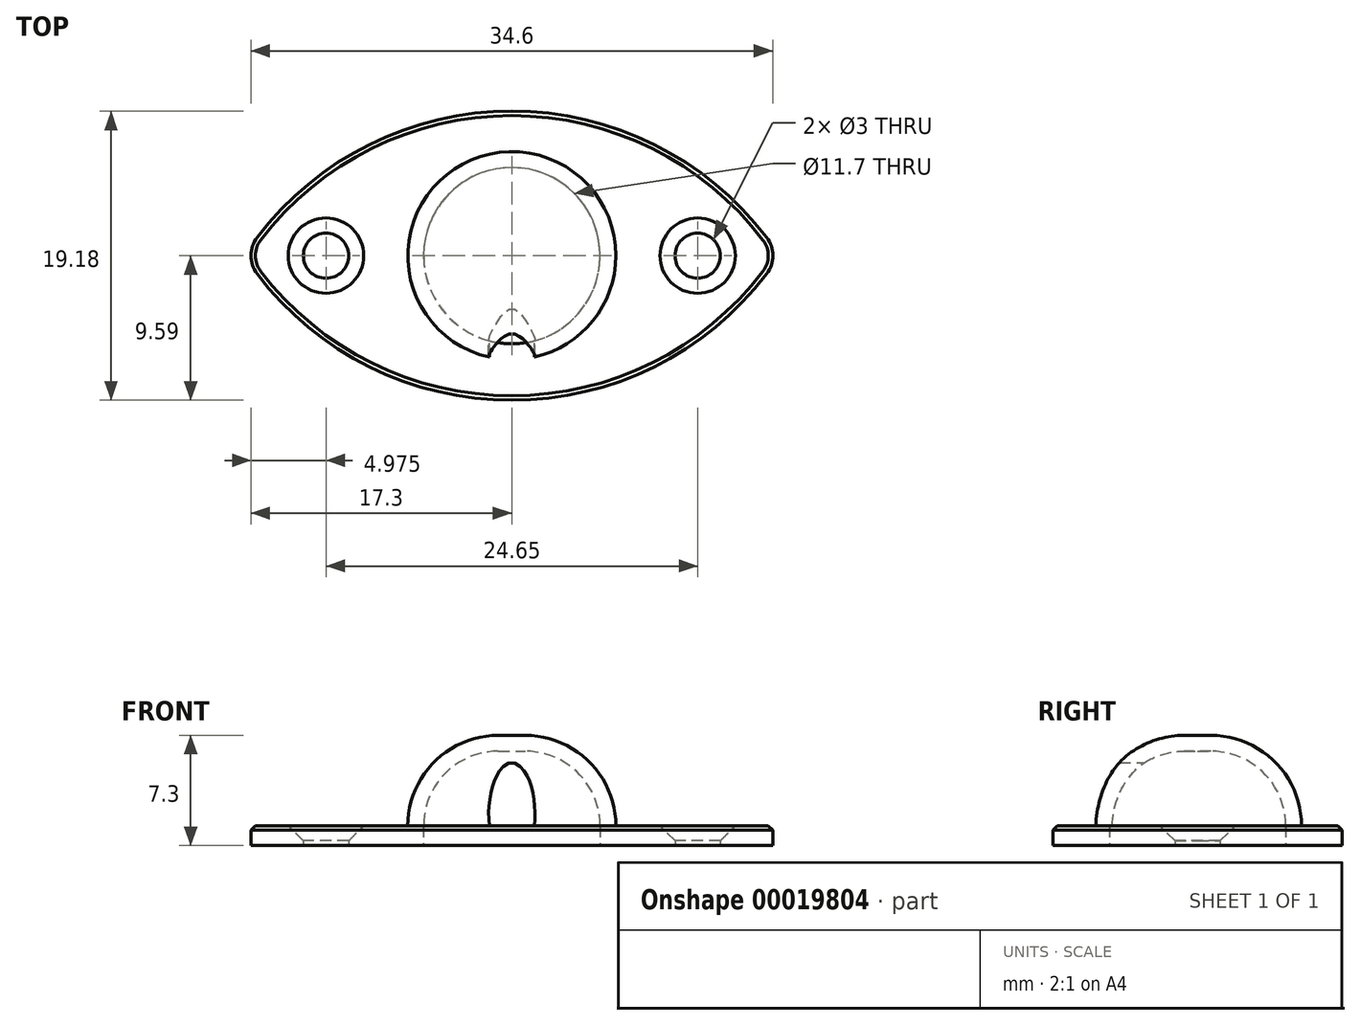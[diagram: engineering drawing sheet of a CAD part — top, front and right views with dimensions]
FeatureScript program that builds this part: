
annotation { "Feature Type Name" : "Feature", "Feature Type Description" : "" }
export const myFeature = defineFeature(function(context is Context, id is Id, definition is map)
    precondition{}
    {
        {
            var Q0;
            Q0=qCreatedBy(makeId("Top.planeOp"),FACE);
            var sketch = newSketch(context, id + "F0", { "sketchPlane" : qUnion([Q0])});
            skArc(sketch, "E0", {"start": v(16.9, 1.2) * mm, "mid": v(0, 9.6) * mm, "end": v(-16.9, 1.2) * mm});
            skLineSegment(sketch, "E1", {"start": v(-17.75, 0) * mm, "end": v(17.75, 0) * mm, "construction": true});
            skArc(sketch, "E2.0.MirrorCS", {"start": v(16.9, -1.2) * mm, "mid": v(0, -9.6) * mm, "end": v(-16.9, -1.2) * mm});
            skCircle(sketch, "E3", {"center": v(0, 0) * mm, "radius": 6.9 * mm});
            skLineSegment(sketch, "E4", {"start": v(-17.75, 0) * mm, "end": v(-6.9, 0) * mm, "construction": true});
            skCircle(sketch, "E5", {"center": v(-12.33, 0) * mm, "radius": 1.5 * mm});
            skLineSegment(sketch, "E6", {"start": v(0, 11.62) * mm, "end": v(0, -11.62) * mm, "construction": true});
            skCircle(sketch, "E7.0.MirrorC", {"center": v(12.33, 0) * mm, "radius": 1.5 * mm});
            skCircle(sketch, "E8", {"center": v(0, 0) * mm, "radius": 5.85 * mm});
            skPoint(sketch, "E9.visualSharp", {"position": v(-17.75, 0) * mm});
            skArc(sketch, "E9.filletArc", {"start": v(-16.9, 1.2) * mm, "mid": v(-17.3, 0) * mm, "end": v(-16.9, -1.2) * mm});
            skPoint(sketch, "E10.visualSharp", {"position": v(17.75, 0) * mm});
            skArc(sketch, "E10.filletArc", {"start": v(16.9, -1.2) * mm, "mid": v(17.3, 0) * mm, "end": v(16.9, 1.2) * mm});
            skSolve(sketch);
        }
        {
            var Q0;
            Q0=makeQuery(id+"F0.imprint","IMPRINT",FACE,{"disambiguationData":[TD([[makeQuery(id+"F0.imprint","IMPRINT",EDGE,{"derivedFrom":sQuery(id+"F0.wireOp",EDGE,"E0")}),1.0]])]});
            extrude(context, id + "F1", {"entities" : qUnion([Q0]), "depth" : 1.3 * mm});
        }
        {
            var Q0;
            Q0=makeQuery(id+"F1.opExtrude","CAP_EDGE",EDGE,{"disambiguationData":[OSD([sQuery(id+"F0.wireOp",EDGE,"E5")])],"isStart":false});
            var Q1;
            Q1=makeQuery(id+"F1.opExtrude","CAP_EDGE",EDGE,{"disambiguationData":[OSD([sQuery(id+"F0.wireOp",EDGE,"E7.0.MirrorC")])],"isStart":false});
            chamfer(context, id + "F2", {"entities" : qUnion([Q0, Q1]), "chamferType" : ChamferType.OFFSET_ANGLE, "width" : 1 * mm, "oppositeDirection" : false, "angle" : 45 * degree, "tangentPropagation" : true});
        }
        {
            var Q0;
            Q0=makeQuery(id+"F1.opExtrude","CAP_EDGE",EDGE,{"disambiguationData":[OSD([sQuery(id+"F0.wireOp",EDGE,"E2.0.MirrorCS")])],"isStart":false});
            var Q1;
            Q1=makeQuery(id+"F1.opExtrude","CAP_EDGE",EDGE,{"disambiguationData":[OSD([sQuery(id+"F0.wireOp",EDGE,"E0")])],"isStart":false});
            chamfer(context, id + "F3", {"entities" : qUnion([Q0, Q1]), "width" : .3 * mm, "tangentPropagation" : true});
        }
        {
            var Q0;
            Q0=makeQuery(id+"F0.imprint","IMPRINT",FACE,{"disambiguationData":[TD([[makeQuery(id+"F0.imprint","IMPRINT",EDGE,{"derivedFrom":sQuery(id+"F0.wireOp",EDGE,"E3")}),1.0]])]});
            var Q1;
            Q1=makeQuery(id+"F0.imprint","IMPRINT",FACE,{"disambiguationData":[TD([[makeQuery(id+"F0.imprint","IMPRINT",EDGE,{"derivedFrom":sQuery(id+"F0.wireOp",EDGE,"E8")}),1.0]])]});
            var Q2;
            Q2=sQuery(id+"F0.wireOp",EDGE,"E3");
            extrude(context, id + "F4", {"entities" : qUnion([Q0, Q1]), "operationType" : NewBodyOperationType.ADD, "surfaceEntities" : qUnion([Q2]), "depth" : 7.3 * mm});
        }
        {
            var Q0;
            Q0=makeQuery(id+"F0.imprint","IMPRINT",FACE,{"disambiguationData":[TD([[makeQuery(id+"F0.imprint","IMPRINT",EDGE,{"derivedFrom":sQuery(id+"F0.wireOp",EDGE,"E8")}),1.0]])]});
            var Q1;
            Q1=makeQuery(id+"F0.imprint","IMPRINT",FACE,{"disambiguationData":[TD([[makeQuery(id+"F0.imprint","IMPRINT",EDGE,{"derivedFrom":sQuery(id+"F0.wireOp",EDGE,"E3")}),1.0]])]});
            extrude(context, id + "F5", {"entities" : qUnion([Q0, Q1]), "operationType" : NewBodyOperationType.ADD, "depth" : 7.3 * mm});
        }
        {
            var Q0;
            Q0=makeQuery(id+"F4.opExtrude","CAP_FACE",FACE,{"disambiguationData":[OSD([sQuery(id+"F0.wireOp",EDGE,"E3")])],"isStart":false});
            fillet(context, id + "F6", {"entities" : qUnion([Q0]), "radius" : 6 * mm, "tangentPropagation" : true, "allowEdgeOverflow" : false});
        }
        {
            var Q0;
            Q0=qCreatedBy(makeId("Front.planeOp"),FACE);
            var Q1;
            Q1=sQuery(id+"F0.wireOp",VERTEX,"E8.center");
            cPlane(context, id + "F7", {"entities" : qUnion([Q0, Q1]), "cplaneType" : CPlaneType.PLANE_POINT, "offset" : 150 * mm, "width" : 150 * mm, "height" : 150 * mm});
        }
        {
            var Q0;
            Q0=qCreatedBy(id+"F7.planeOp",FACE);
            var sketch = newSketch(context, id + "F8", { "sketchPlane" : qUnion([Q0])});
            skLineSegment(sketch, "E11", {"start": v(-5.85, 0) * mm, "end": v(-5.85, 1.3) * mm});
            skLineSegment(sketch, "E12", {"start": v(5.85, 0) * mm, "end": v(5.85, 1.3) * mm});
            skArc(sketch, "E13", {"start": v(-0.9, 6.25) * mm, "mid": v(-4.4, 4.8) * mm, "end": v(-5.85, 1.3) * mm});
            skArc(sketch, "E14", {"start": v(5.85, 1.3) * mm, "mid": v(4.4, 4.8) * mm, "end": v(0.9, 6.25) * mm});
            skLineSegment(sketch, "E15", {"start": v(-0.9, 6.25) * mm, "end": v(0.9, 6.25) * mm});
            skLineSegment(sketch, "E16", {"start": v(0, 0) * mm, "end": v(0, 6.25) * mm});
            skLineSegment(sketch, "E17", {"start": v(-5.85, 0) * mm, "end": v(0, 0) * mm});
            skSolve(sketch);
        }
        {
            var Q0;
            Q0=qSketchRegion(id+"F8",true);
            var Q1;
            Q1=sQuery(id+"F8.wireOp",EDGE,"E16");
            revolve(context, id + "F9", {"operationType" : NewBodyOperationType.REMOVE, "entities" : qUnion([Q0]), "axis" : qUnion([Q1]), "revolveType" : RevolveType.FULL});
        }
        {
            var Q0;
            Q0=qCreatedBy(id+"F7.planeOp",FACE);
            var sketch = newSketch(context, id + "F10", { "sketchPlane" : qUnion([Q0])});
            skLineSegment(sketch, "E18", {"start": v(-1.5, 1.3) * mm, "end": v(1.5, 1.3) * mm});
            skPoint(sketch, "E19", {"position": v(0, 1.3) * mm});
            skFitSpline(sketch, "E20", {"points": [v(-1.5, 1.3) * mm, v(0, 5.5) * mm, v(1.5, 1.3) * mm], "startDerivative": vector(-1.29, 14.4) * mm, "endDerivative": vector(-1.29, -14.4) * mm});
            skLineSegment(sketch, "E21", {"start": v(0, 1.3) * mm, "end": v(0, 5.5) * mm, "construction": true});
            skSolve(sketch);
        }
        {
            var Q0;
            Q0=qSketchRegion(id+"F10",true);
            var Q1;
            Q1=makeQuery(id+"F6.opFillet","BLEND_FACE",FACE,{"disambiguationData":[OSD([sQuery(id+"F0.wireOp",EDGE,"E3")])]});
            extrude(context, id + "F11", {"entities" : qUnion([Q0]), "operationType" : NewBodyOperationType.REMOVE, "endBound" : BoundingType.UP_TO_SURFACE, "endBoundEntityFace" : qUnion([Q1]), "depth" : 25 * mm});
        }
    });
